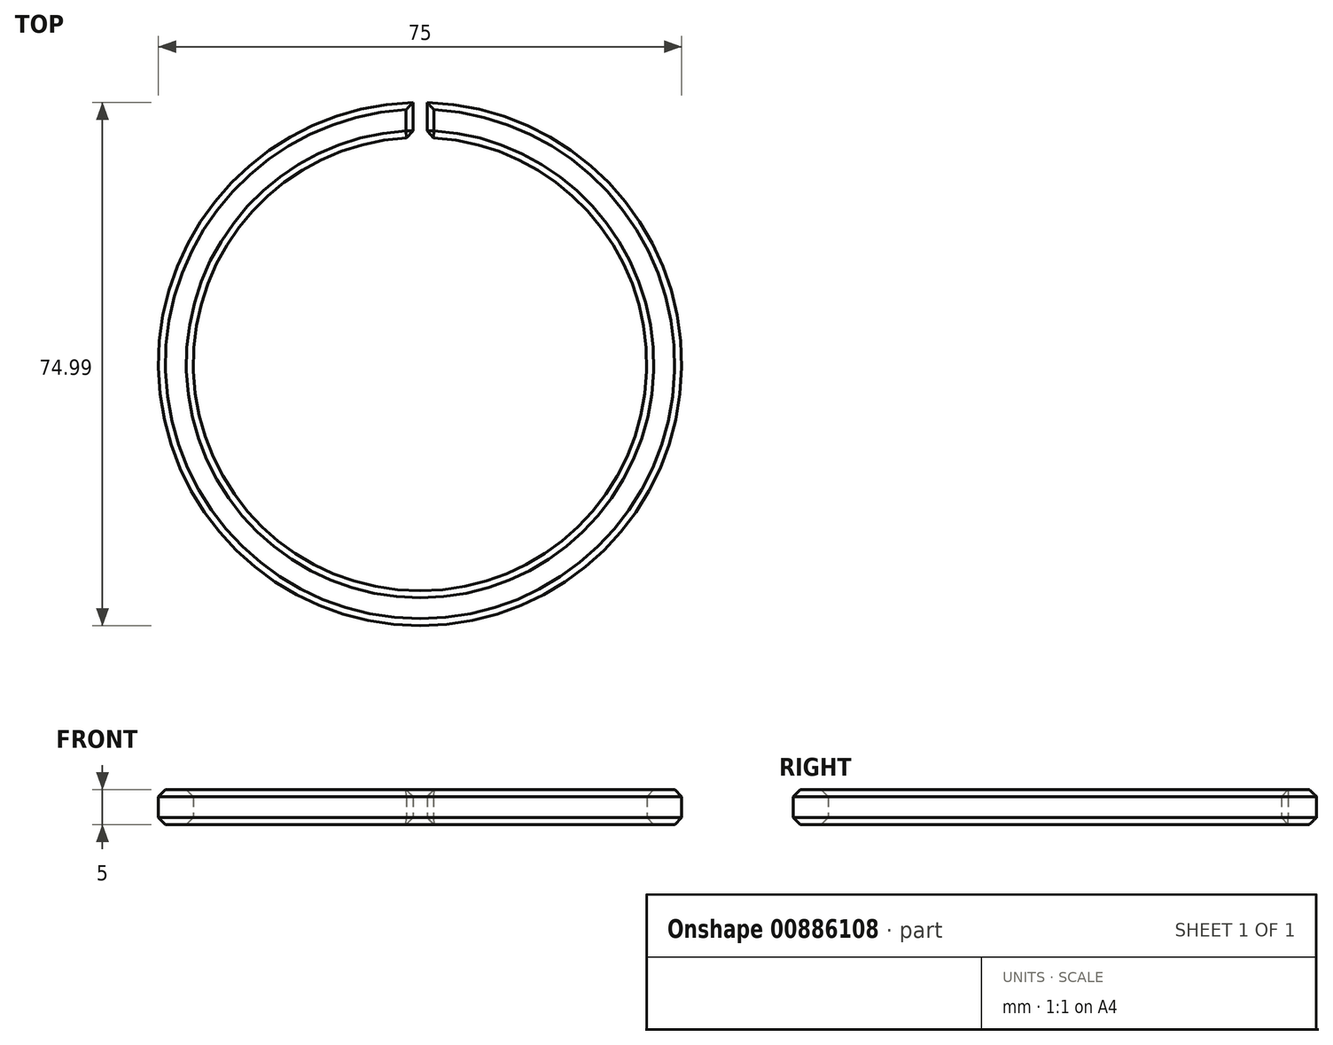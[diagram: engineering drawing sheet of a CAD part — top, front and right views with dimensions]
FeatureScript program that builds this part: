
annotation { "Feature Type Name" : "Feature", "Feature Type Description" : "" }
export const myFeature = defineFeature(function(context is Context, id is Id, definition is map)
    precondition{}
    {
        {
            var Q0;
            Q0=qCreatedBy(makeId("Top.planeOp"),FACE);
            var sketch = newSketch(context, id + "F0", { "sketchPlane" : qUnion([Q0])});
            skCircle(sketch, "E0", {"center": v(0, 0) * mm, "radius": 32.5 * mm});
            skCircle(sketch, "E1", {"center": v(0, 0) * mm, "radius": 37.5 * mm});
            skLineSegment(sketch, "E2.bottom", {"start": v(-1, 47.95) * mm, "end": v(1, 47.95) * mm});
            skLineSegment(sketch, "E2.top", {"start": v(-1, 0.05) * mm, "end": v(1, 0.05) * mm});
            skLineSegment(sketch, "E2.left", {"start": v(-1, 47.95) * mm, "end": v(-1, 0.05) * mm});
            skLineSegment(sketch, "E2.right", {"start": v(1, 47.95) * mm, "end": v(1, 0.05) * mm});
            skPoint(sketch, "E2.middle", {"position": v(0, 24) * mm});
            skSolve(sketch);
        }
        {
            var Q0;
            {var subQ0=sQuery(id+"F0.wireOp",EDGE,"E2.left");var subQ1=sQuery(id+"F0.wireOp",EDGE,"E0");var subQ2=makeQuery(id+"F0.imprint","INTERSECT",VERTEX,{"derivedFrom":[subQ1,subQ0]});Q0=makeQuery(id+"F0.imprint","IMPRINT",FACE,{"disambiguationData":[TD([[makeQuery(id+"F0.imprint","IMPRINT",EDGE,{"disambiguationData":[TD([[subQ2,-1.0]])],"derivedFrom":subQ1}),-1.0]])]});}
            extrude(context, id + "F1", {"entities" : qUnion([Q0]), "depth" : 5 * mm, "offsetDistance" : 25 * mm});
        }
        {
            var Q0;
            Q0=makeQuery(id+"F1.opExtrude","CAP_EDGE",EDGE,{"disambiguationData":[OSD([sQuery(id+"F0.wireOp",EDGE,"E1")])],"isStart":false});
            var Q1;
            Q1=makeQuery(id+"F1.opExtrude","SWEPT_FACE",FACE,{"disambiguationData":[OSD([sQuery(id+"F0.wireOp",EDGE,"E0")])]});
            var Q2;
            Q2=makeQuery(id+"F1.opExtrude","CAP_EDGE",EDGE,{"disambiguationData":[OSD([sQuery(id+"F0.wireOp",EDGE,"E1")])],"isStart":true});
            var Q3;
            Q3=makeQuery(id+"F1.opExtrude","CAP_EDGE",EDGE,{"disambiguationData":[OSD([sQuery(id+"F0.wireOp",EDGE,"E0")])],"isStart":true});
            var Q4;
            Q4=makeQuery(id+"F1.opExtrude","CAP_EDGE",EDGE,{"disambiguationData":[OSD([sQuery(id+"F0.wireOp",EDGE,"E2.left")])],"isStart":false});
            var Q5;
            Q5=makeQuery(id+"F1.opExtrude","CAP_EDGE",EDGE,{"disambiguationData":[OSD([sQuery(id+"F0.wireOp",EDGE,"E2.left")])],"isStart":true});
            var Q6;
            Q6=makeQuery(id+"F1.opExtrude","CAP_EDGE",EDGE,{"disambiguationData":[OSD([sQuery(id+"F0.wireOp",EDGE,"E2.right")])],"isStart":false});
            var Q7;
            Q7=makeQuery(id+"F1.opExtrude","CAP_EDGE",EDGE,{"disambiguationData":[OSD([sQuery(id+"F0.wireOp",EDGE,"E2.right")])],"isStart":true});
            chamfer(context, id + "F2", {"entities" : qUnion([Q0, Q1, Q2, Q3, Q4, Q5, Q6, Q7]), "width" : 1 * mm, "tangentPropagation" : true});
        }
    });
